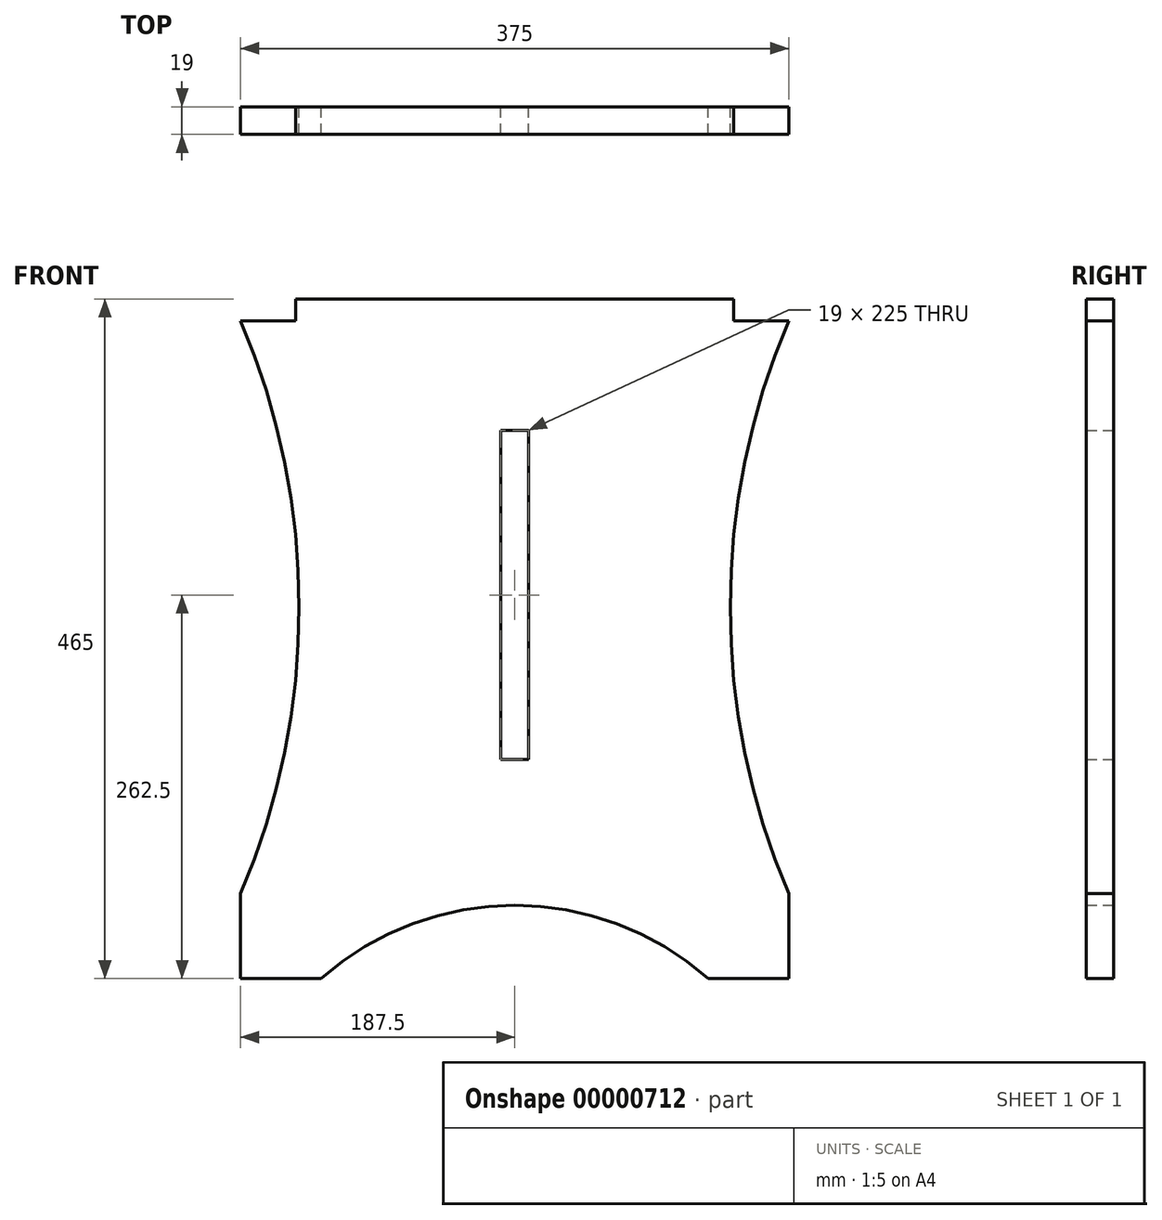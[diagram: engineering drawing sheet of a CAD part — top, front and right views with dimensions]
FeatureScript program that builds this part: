
annotation { "Feature Type Name" : "Feature", "Feature Type Description" : "" }
export const myFeature = defineFeature(function(context is Context, id is Id, definition is map)
    precondition{}
    {
        {
            var Q0;
            Q0=qCreatedBy(makeId("Front.planeOp"),FACE);
            var sketch = newSketch(context, id + "F0", { "sketchPlane" : qUnion([Q0])});
            skLineSegment(sketch, "E0", {"start": v(-150, 15) * mm, "end": v(150, 15) * mm});
            skLineSegment(sketch, "E1", {"start": v(0, 0) * mm, "end": v(0, 15) * mm, "construction": true});
            skLineSegment(sketch, "E2", {"start": v(-150, 15) * mm, "end": v(-150, 0) * mm});
            skLineSegment(sketch, "E3", {"start": v(-150, 0) * mm, "end": v(-187.5, 0) * mm});
            skLineSegment(sketch, "E4", {"start": v(-187.5, -391.92) * mm, "end": v(-187.5, -450) * mm});
            skLineSegment(sketch, "E5", {"start": v(-187.5, -450) * mm, "end": v(-132.5, -450) * mm});
            skLineSegment(sketch, "E6", {"start": v(150, 15) * mm, "end": v(150, 0) * mm});
            skLineSegment(sketch, "E7", {"start": v(150, 0) * mm, "end": v(187.5, 0) * mm});
            skLineSegment(sketch, "E8", {"start": v(187.5, -391.92) * mm, "end": v(187.5, -450) * mm});
            skLineSegment(sketch, "E9", {"start": v(187.5, -450) * mm, "end": v(132.5, -450) * mm});
            skArc(sketch, "E10", {"start": v(132.5, -450) * mm, "mid": v(0, -399.81) * mm, "end": v(-132.5, -450) * mm});
            skLineSegment(sketch, "E11.rect.bottom", {"start": v(9.5, -300) * mm, "end": v(-9.5, -300) * mm});
            skLineSegment(sketch, "E11.rect.top", {"start": v(9.5, -75) * mm, "end": v(-9.5, -75) * mm});
            skLineSegment(sketch, "E11.rect.left", {"start": v(9.5, -300) * mm, "end": v(9.5, -75) * mm});
            skLineSegment(sketch, "E11.rect.right", {"start": v(-9.5, -300) * mm, "end": v(-9.5, -75) * mm});
            skPoint(sketch, "E11.rect.middle", {"position": v(0, -187.5) * mm});
            skLineSegment(sketch, "E12", {"start": v(0, -187.5) * mm, "end": v(0, 0) * mm, "construction": true});
            skArc(sketch, "E13", {"start": v(-187.5, -391.92) * mm, "mid": v(-147.5, -195.96) * mm, "end": v(-187.5, 0) * mm});
            skArc(sketch, "E14", {"start": v(187.5, 0) * mm, "mid": v(147.5, -195.96) * mm, "end": v(187.5, -391.92) * mm});
            skSolve(sketch);
        }
        {
            var Q0;
            Q0=makeQuery(id+"F0.imprint","IMPRINT",FACE,{"disambiguationData":[TD([[makeQuery(id+"F0.imprint","IMPRINT",EDGE,{"derivedFrom":sQuery(id+"F0.wireOp",EDGE,"E0")}),-1.0]])]});
            extrude(context, id + "F1", {"entities" : qUnion([Q0]), "depth" : 19 * mm});
        }
    });
